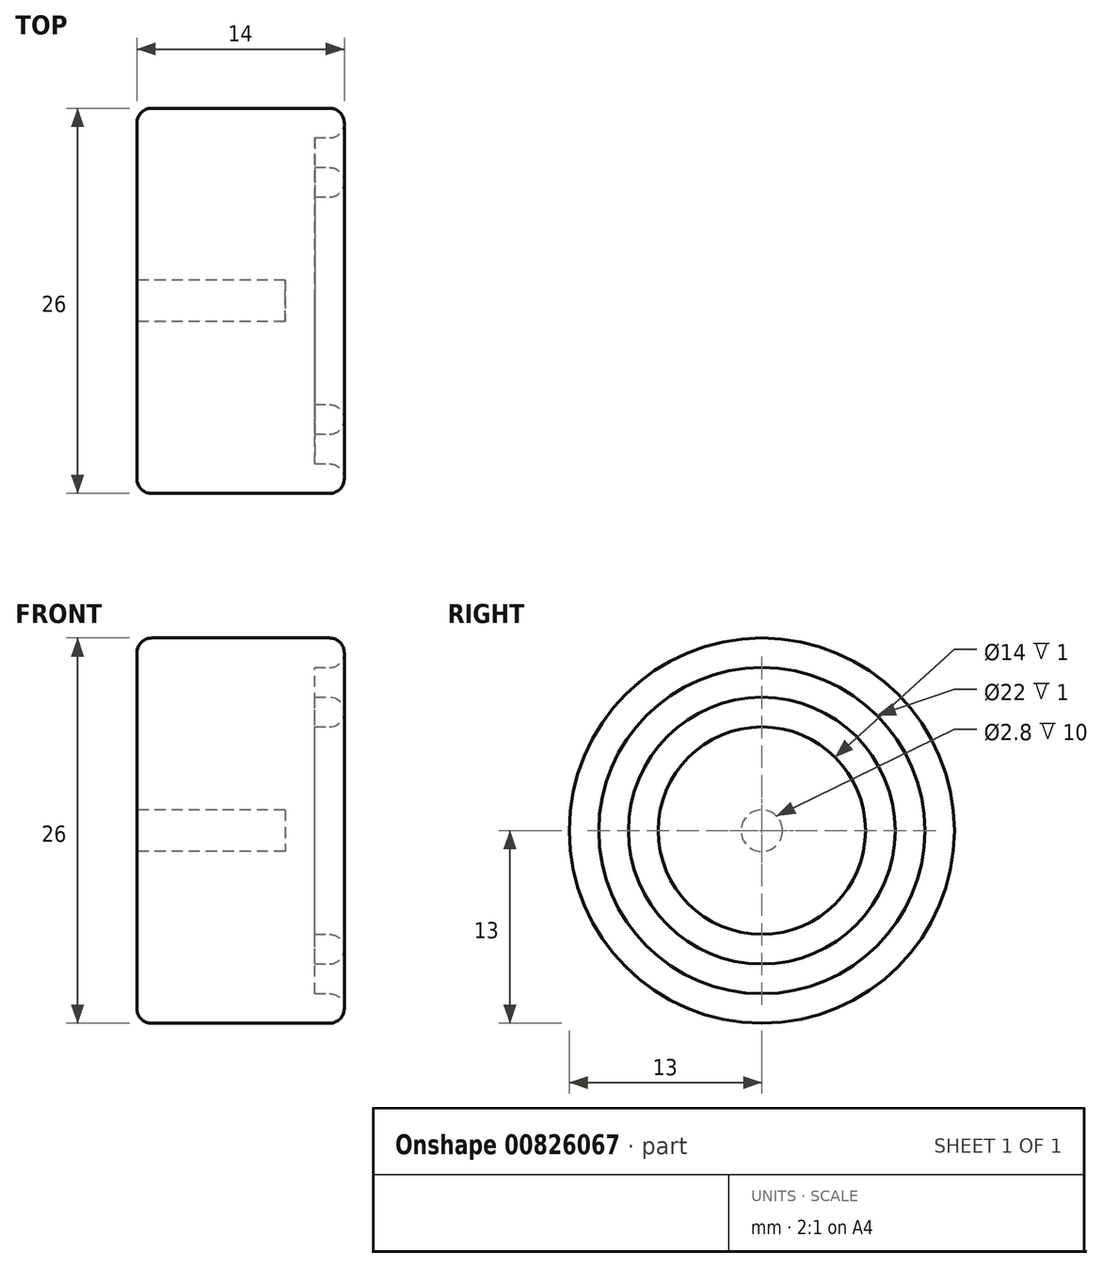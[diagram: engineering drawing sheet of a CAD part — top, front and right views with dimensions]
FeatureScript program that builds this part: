
annotation { "Feature Type Name" : "Feature", "Feature Type Description" : "" }
export const myFeature = defineFeature(function(context is Context, id is Id, definition is map)
    precondition{}
    {
        {
            var Q0;
            Q0=qCreatedBy(makeId("Front.planeOp"),FACE);
            var sketch = newSketch(context, id + "F0", { "sketchPlane" : qUnion([Q0])});
            skLineSegment(sketch, "E0.bottom", {"start": v(0, 0) * mm, "end": v(-12, 0) * mm});
            skLineSegment(sketch, "E0.top", {"start": v(0, 13) * mm, "end": v(-12, 13) * mm});
            skLineSegment(sketch, "E0.left", {"start": v(0, 0) * mm, "end": v(0, 13) * mm});
            skLineSegment(sketch, "E0.right", {"start": v(-12, 0) * mm, "end": v(-12, 13) * mm});
            skLineSegment(sketch, "E1.bottom", {"start": v(2, 13) * mm, "end": v(-12, 13) * mm});
            skLineSegment(sketch, "E1.top", {"start": v(2, 11) * mm, "end": v(-12, 11) * mm});
            skLineSegment(sketch, "E1.left", {"start": v(2, 13) * mm, "end": v(2, 11) * mm});
            skLineSegment(sketch, "E2", {"start": v(4.7, 11) * mm, "end": v(4.7, 12.75) * mm, "construction": true});
            skLineSegment(sketch, "E3", {"start": v(8.15, 11) * mm, "end": v(8.15, 9) * mm, "construction": true});
            skLineSegment(sketch, "E4.bottom", {"start": v(0, 9) * mm, "end": v(2, 9) * mm});
            skLineSegment(sketch, "E4.top", {"start": v(0, 7) * mm, "end": v(2, 7) * mm});
            skLineSegment(sketch, "E4.left", {"start": v(0, 9) * mm, "end": v(0, 7) * mm});
            skLineSegment(sketch, "E4.right", {"start": v(2, 9) * mm, "end": v(2, 7) * mm});
            skPoint(sketch, "E5.orphan", {"position": v(-14, 13) * mm});
            skSolve(sketch);
        }
        {
            var Q0;
            Q0 = qSketchRegion(id + "F0", true);
            var Q1;
            Q1=sQuery(id+"F0.wireOp",EDGE,"E0.bottom");
            revolve(context, id + "F1", {"surfaceOperationType" : NewSurfaceOperationType.NEW, "entities" : qUnion([Q0]), "axis" : qUnion([Q1]), "revolveType" : RevolveType.FULL});
        }
        {
            var Q0;
            Q0=makeQuery(id+"F1.opRevolve","SWEPT_EDGE",EDGE,{"disambiguationData":[OSD([sQuery(id+"F0.wireOp",EDGE,"E1.bottom"),sQuery(id+"F0.wireOp",EDGE,"E1.left")])]});
            var Q1;
            Q1=makeQuery(id+"F1.opRevolve","SWEPT_EDGE",EDGE,{"disambiguationData":[OSD([sQuery(id+"F0.wireOp",EDGE,"E4.bottom"),sQuery(id+"F0.wireOp",EDGE,"E4.right")])]});
            var Q2;
            Q2=makeQuery(id+"F1.opRevolve","SWEPT_EDGE",EDGE,{"disambiguationData":[OSD([sQuery(id+"F0.wireOp",EDGE,"E4.top"),sQuery(id+"F0.wireOp",EDGE,"E4.right")])]});
            var Q3;
            Q3=makeQuery(id+"F1.opRevolve","SWEPT_EDGE",EDGE,{"disambiguationData":[OSD([sQuery(id+"F0.wireOp",EDGE,"E1.top"),sQuery(id+"F0.wireOp",EDGE,"E1.left")])]});
            var Q4;
            Q4=makeQuery(id+"F1.opRevolve","SWEPT_EDGE",EDGE,{"disambiguationData":[OSD([sQuery(id+"F0.wireOp",EDGE,"E0.right"),sQuery(id+"F0.wireOp",EDGE,"E1.bottom")])]});
            fillet(context, id + "F2", {"entities" : qUnion([Q0, Q1, Q2, Q3, Q4]), "radius" : 1 * mm, "tangentPropagation" : true, "allowEdgeOverflow" : false});
        }
        {
            var Q0;
            Q0=makeQuery(id+"F1.opRevolve","SWEPT_FACE",FACE,{"disambiguationData":[OSD([sQuery(id+"F0.wireOp",EDGE,"E0.right")])]});
            var sketch = newSketch(context, id + "F3", { "sketchPlane" : qUnion([Q0])});
            skCircle(sketch, "E6", {"center": v(0, 0) * mm, "radius": 1.4 * mm});
            skSolve(sketch);
        }
        {
            var Q0;
            Q0=makeQuery(id+"F3.imprint","IMPRINT",FACE,{"disambiguationData":[TD([[makeQuery(id+"F3.imprint","IMPRINT",EDGE,{"derivedFrom":sQuery(id+"F3.wireOp",EDGE,"E6")}),1.0]])]});
            extrude(context, id + "F4", {"entities" : qUnion([Q0]), "operationType" : NewBodyOperationType.REMOVE, "oppositeDirection" : true, "depth" : 10 * mm, "offsetDistance" : 25 * mm});
        }
    });
